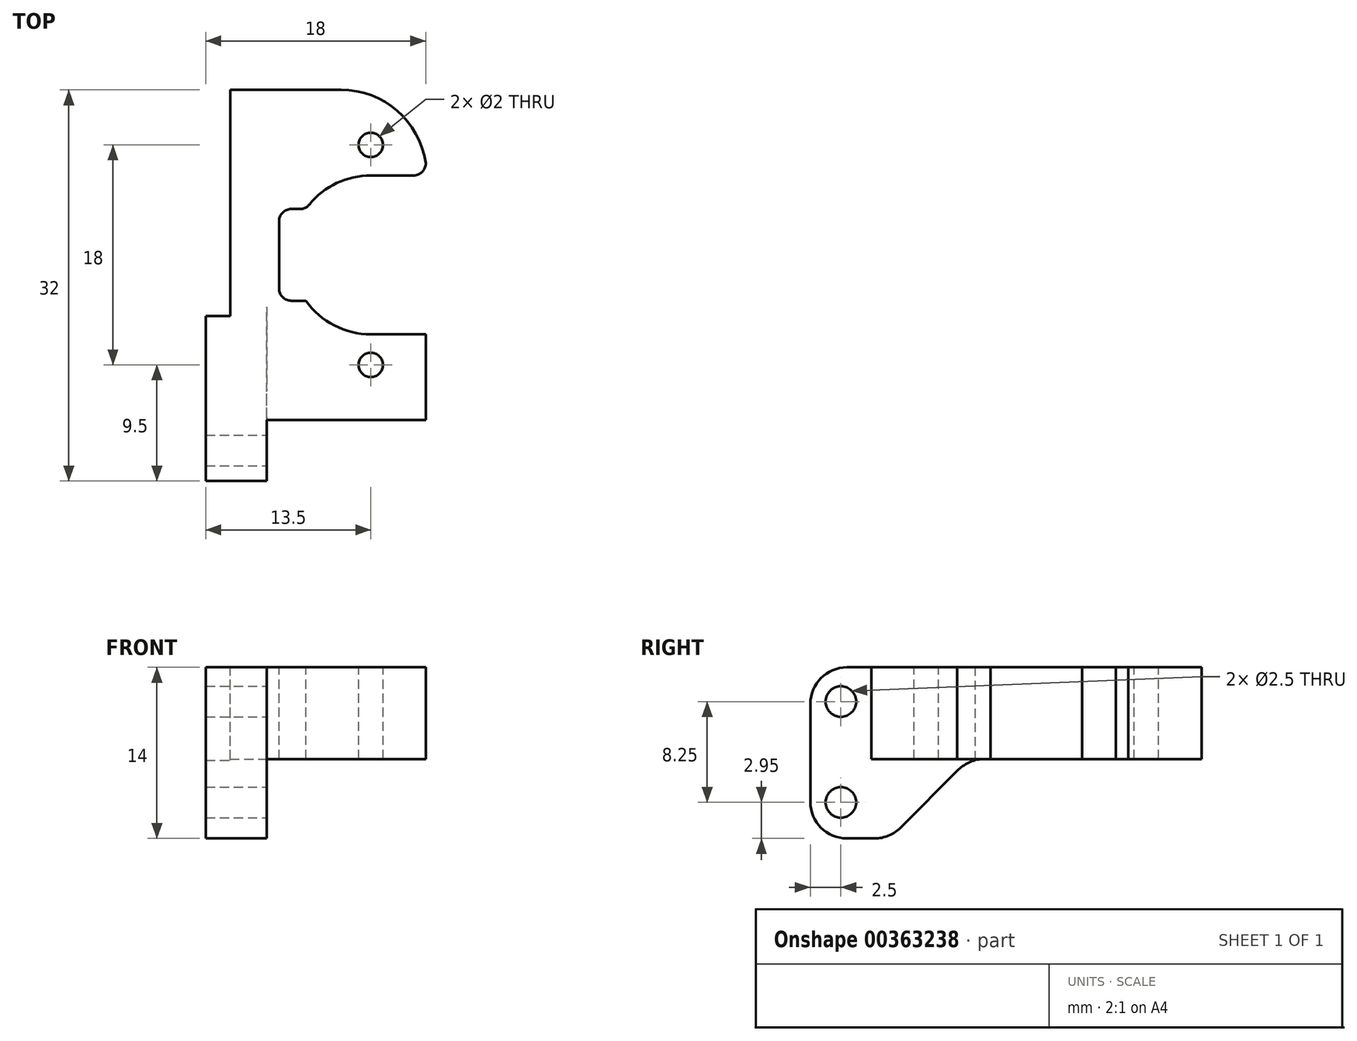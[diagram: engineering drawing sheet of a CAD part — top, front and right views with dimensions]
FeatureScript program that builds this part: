
annotation { "Feature Type Name" : "Feature", "Feature Type Description" : "" }
export const myFeature = defineFeature(function(context is Context, id is Id, definition is map)
    precondition{}
    {
        {
            var Q0;
            Q0=qCreatedBy(makeId("Top.planeOp"),FACE);
            var sketch = newSketch(context, id + "F0", { "sketchPlane" : qUnion([Q0])});
            skLineSegment(sketch, "E0.bottom", {"start": v(0, 0) * mm, "end": v(18, 0) * mm});
            skLineSegment(sketch, "E0.top", {"start": v(0, 32) * mm, "end": v(18, 32) * mm});
            skLineSegment(sketch, "E0.left", {"start": v(0, 0) * mm, "end": v(0, 32) * mm});
            skLineSegment(sketch, "E0.right", {"start": v(18, 0) * mm, "end": v(18, 32) * mm});
            skSolve(sketch);
        }
        {
            var Q0;
            Q0=qSketchRegion(id+"F0",true);
            extrude(context, id + "F1", {"entities" : qUnion([Q0]), "depth" : 14 * mm});
        }
        {
            var Q0;
            Q0=makeQuery(id+"F1.opExtrude","CAP_FACE",FACE,{"disambiguationData":[OSD([sQuery(id+"F0.wireOp",EDGE,"E0.bottom"),sQuery(id+"F0.wireOp",EDGE,"E0.top"),sQuery(id+"F0.wireOp",EDGE,"E0.left"),sQuery(id+"F0.wireOp",EDGE,"E0.right")])],"isStart":false});
            var sketch = newSketch(context, id + "F2", { "sketchPlane" : qUnion([Q0])});
            skLineSegment(sketch, "E1.bottom", {"start": v(5, 0) * mm, "end": v(18, 0) * mm});
            skLineSegment(sketch, "E1.top", {"start": v(5, 5) * mm, "end": v(18, 5) * mm});
            skLineSegment(sketch, "E1.left", {"start": v(5, 0) * mm, "end": v(5, 5) * mm});
            skLineSegment(sketch, "E1.right", {"start": v(18, 0) * mm, "end": v(18, 5) * mm});
            skLineSegment(sketch, "E2.bottom", {"start": v(0, 32) * mm, "end": v(2, 32) * mm});
            skLineSegment(sketch, "E2.top", {"start": v(0, 13.5) * mm, "end": v(2, 13.5) * mm});
            skLineSegment(sketch, "E2.left", {"start": v(0, 32) * mm, "end": v(0, 13.5) * mm});
            skLineSegment(sketch, "E2.right", {"start": v(2, 32) * mm, "end": v(2, 13.5) * mm});
            skSolve(sketch);
        }
        {
            var Q0;
            Q0=qSketchRegion(id+"F2",true);
            extrude(context, id + "F3", {"entities" : qUnion([Q0]), "operationType" : NewBodyOperationType.REMOVE, "endBound" : BoundingType.UP_TO_NEXT, "oppositeDirection" : true, "depth" : 25 * mm});
        }
        {
            var Q0;
            Q0=makeQuery(id+"F1.opExtrude","SWEPT_FACE",FACE,{"disambiguationData":[OSD([sQuery(id+"F0.wireOp",EDGE,"E0.right")])]});
            var sketch = newSketch(context, id + "F4", { "sketchPlane" : qUnion([Q0])});
            skLineSegment(sketch, "E3.bottom", {"start": v(5, 0) * mm, "end": v(32, 0) * mm});
            skLineSegment(sketch, "E3.top", {"start": v(5, 6.5) * mm, "end": v(32, 6.5) * mm});
            skLineSegment(sketch, "E3.left", {"start": v(5, 0) * mm, "end": v(5, 6.5) * mm});
            skLineSegment(sketch, "E3.right", {"start": v(32, 0) * mm, "end": v(32, 6.5) * mm});
            skSolve(sketch);
        }
        {
            var Q0;
            Q0=qSketchRegion(id+"F4",true);
            extrude(context, id + "F5", {"entities" : qUnion([Q0]), "operationType" : NewBodyOperationType.REMOVE, "endBound" : BoundingType.UP_TO_NEXT, "oppositeDirection" : true, "depth" : 25 * mm});
        }
        {
            var Q0;
            Q0=makeQuery(id+"F1.opExtrude","CAP_FACE",FACE,{"disambiguationData":[OSD([sQuery(id+"F0.wireOp",EDGE,"E0.bottom"),sQuery(id+"F0.wireOp",EDGE,"E0.top"),sQuery(id+"F0.wireOp",EDGE,"E0.left"),sQuery(id+"F0.wireOp",EDGE,"E0.right")])],"isStart":false});
            var sketch = newSketch(context, id + "F6", { "sketchPlane" : qUnion([Q0])});
            skLineSegment(sketch, "E4", {"start": v(13.5, 32) * mm, "end": v(13.5, 5) * mm, "construction": true});
            skCircle(sketch, "E5", {"center": v(13.5, 27.5) * mm, "radius": 1 * mm});
            skCircle(sketch, "E6", {"center": v(13.5, 9.5) * mm, "radius": 1 * mm});
            skCircle(sketch, "E7", {"center": v(13.5, 18.5) * mm, "radius": 6.5 * mm});
            skPoint(sketch, "E8", {"position": v(13.5, 25) * mm});
            skPoint(sketch, "E9", {"position": v(13.5, 12) * mm});
            skLineSegment(sketch, "E10", {"start": v(13.5, 25) * mm, "end": v(18, 25) * mm});
            skLineSegment(sketch, "E11", {"start": v(18, 25) * mm, "end": v(18, 12) * mm});
            skLineSegment(sketch, "E12", {"start": v(18, 12) * mm, "end": v(13.5, 12) * mm});
            skSolve(sketch);
        }
        {
            var Q0;
            Q0=makeQuery(id+"F6.imprint","IMPRINT",FACE,{"disambiguationData":[TD([[makeQuery(id+"F6.imprint","IMPRINT",EDGE,{"derivedFrom":sQuery(id+"F6.wireOp",EDGE,"E6")}),1.0]])]});
            var Q1;
            Q1=makeQuery(id+"F6.imprint","IMPRINT",FACE,{"disambiguationData":[TD([[makeQuery(id+"F6.imprint","IMPRINT",EDGE,{"derivedFrom":sQuery(id+"F6.wireOp",EDGE,"E7")}),1.0]])]});
            var Q2;
            Q2=makeQuery(id+"F6.imprint","IMPRINT",FACE,{"disambiguationData":[TD([[makeQuery(id+"F6.imprint","IMPRINT",EDGE,{"derivedFrom":sQuery(id+"F6.wireOp",EDGE,"E5")}),1.0]])]});
            var Q3;
            {var subQ0=sQuery(id+"F6.wireOp",EDGE,"E10");Q3=makeQuery(id+"F6.imprint","IMPRINT",FACE,{"disambiguationData":[TD([[makeQuery(id+"F6.imprint","IMPRINT",EDGE,{"derivedFrom":subQ0}),-1.0]])]});}
            var Q4;
            {var subQ0=sQuery(id+"F6.wireOp",EDGE,"E12");Q4=makeQuery(id+"F6.imprint","IMPRINT",FACE,{"disambiguationData":[TD([[makeQuery(id+"F6.imprint","IMPRINT",EDGE,{"derivedFrom":subQ0}),-1.0]])]});}
            extrude(context, id + "F7", {"entities" : qUnion([Q0, Q1, Q2, Q3, Q4]), "operationType" : NewBodyOperationType.REMOVE, "endBound" : BoundingType.UP_TO_NEXT, "oppositeDirection" : true, "depth" : 25 * mm});
        }
        {
            var Q0;
            Q0=makeQuery(id+"F3.boolean.opBoolean","COPY",FACE,{"derivedFrom":makeQuery(id+"F3.opExtrude","SWEPT_FACE",FACE,{"disambiguationData":[OSD([sQuery(id+"F2.wireOp",EDGE,"E1.left")])]})});
            var sketch = newSketch(context, id + "F8", { "sketchPlane" : qUnion([Q0])});
            skCircle(sketch, "E13", {"center": v(2.5, 11.2) * mm, "radius": 1.25 * mm});
            skPoint(sketch, "E13.centerSnap0", {"position": v(2.5, 14) * mm});
            skCircle(sketch, "E14", {"center": v(2.5, 2.95) * mm, "radius": 1.25 * mm});
            skPoint(sketch, "E14.centerSnap0", {"position": v(2.5, 0) * mm});
            skSolve(sketch);
        }
        {
            var Q0;
            Q0=qSketchRegion(id+"F8",true);
            extrude(context, id + "F9", {"entities" : qUnion([Q0]), "operationType" : NewBodyOperationType.REMOVE, "endBound" : BoundingType.UP_TO_NEXT, "oppositeDirection" : true, "depth" : 25 * mm});
        }
        {
            var Q0;
            {var subQ0=sQuery(id+"F4.wireOp",EDGE,"E3.top");var subQ1=sQuery(id+"F2.wireOp",EDGE,"E1.top");var subQ2=sQuery(id+"F4.wireOp",EDGE,"E3.left");Q0=makeQuery(id+"F5.boolean.opBoolean","COPY",EDGE,{"disambiguationData":[TD([makeQuery(id+"F1.opExtrude","SWEPT_FACE",FACE,{"disambiguationData":[OSD([sQuery(id+"F0.wireOp",EDGE,"E0.left")])]})])],"derivedFrom":makeQuery(id+"F5.opExtrude","SWEPT_EDGE",EDGE,{"disambiguationData":[OSD([sQuery(id+"F0.wireOp",EDGE,"E0.right"),subQ1,sQuery(id+"F2.wireOp",EDGE,"E1.right"),subQ0,subQ2])]})});}
            chamfer(context, id + "F10", {"entities" : qUnion([Q0]), "width" : 8 * mm, "tangentPropagation" : true});
        }
        {
            var Q0;
            Q0=makeQuery(id+"F1.opExtrude","CAP_EDGE",EDGE,{"disambiguationData":[OSD([sQuery(id+"F0.wireOp",EDGE,"E0.bottom")])],"isStart":false});
            var Q1;
            Q1=makeQuery(id+"F1.opExtrude","CAP_EDGE",EDGE,{"disambiguationData":[OSD([sQuery(id+"F0.wireOp",EDGE,"E0.bottom")])],"isStart":true});
            var Q2;
            {var subQ0=sQuery(id+"F0.wireOp",EDGE,"E0.right");var subQ1=sQuery(id+"F0.wireOp",EDGE,"E0.left");var subQ2=sQuery(id+"F4.wireOp",EDGE,"E3.top");var subQ3=sQuery(id+"F2.wireOp",EDGE,"E1.top");var subQ4=sQuery(id+"F4.wireOp",EDGE,"E3.left");Q2=makeQuery(id+"F10.opChamfer","BLEND_EDGE",EDGE,{"blendedFrom":[makeQuery(id+"F5.boolean.opBoolean","COPY",EDGE,{"disambiguationData":[TD([makeQuery(id+"F1.opExtrude","SWEPT_FACE",FACE,{"disambiguationData":[OSD([subQ1])]})])],"derivedFrom":makeQuery(id+"F5.opExtrude","SWEPT_EDGE",EDGE,{"disambiguationData":[OSD([subQ0,subQ3,sQuery(id+"F2.wireOp",EDGE,"E1.right"),subQ2,subQ4])]})}),makeQuery(id+"F1.opExtrude","CAP_FACE",FACE,{"disambiguationData":[OSD([sQuery(id+"F0.wireOp",EDGE,"E0.bottom"),sQuery(id+"F0.wireOp",EDGE,"E0.top"),subQ1,subQ0])],"isStart":true})],"blendedInto":[makeQuery(id+"F1.opExtrude","CAP_FACE",FACE,{"disambiguationData":[OSD([sQuery(id+"F0.wireOp",EDGE,"E0.bottom"),sQuery(id+"F0.wireOp",EDGE,"E0.top"),subQ1,subQ0])],"isStart":true})]});}
            var Q3;
            {var subQ0=sQuery(id+"F4.wireOp",EDGE,"E3.top");var subQ1=makeQuery(id+"F5.opExtrude","SWEPT_FACE",FACE,{"disambiguationData":[OSD([subQ0])]});var subQ2=sQuery(id+"F2.wireOp",EDGE,"E1.top");var subQ3=sQuery(id+"F4.wireOp",EDGE,"E3.left");Q3=makeQuery(id+"F10.opChamfer","BLEND_EDGE",EDGE,{"blendedFrom":[makeQuery(id+"F5.boolean.opBoolean","COPY",EDGE,{"disambiguationData":[TD([makeQuery(id+"F1.opExtrude","SWEPT_FACE",FACE,{"disambiguationData":[OSD([sQuery(id+"F0.wireOp",EDGE,"E0.left")])]})])],"derivedFrom":makeQuery(id+"F5.opExtrude","SWEPT_EDGE",EDGE,{"disambiguationData":[OSD([sQuery(id+"F0.wireOp",EDGE,"E0.right"),subQ2,sQuery(id+"F2.wireOp",EDGE,"E1.right"),subQ0,subQ3])]})}),makeQuery(id+"F5.boolean.opBoolean","COPY",FACE,{"derivedFrom":subQ1})],"blendedInto":[makeQuery(id+"F5.boolean.opBoolean","COPY",FACE,{"derivedFrom":subQ1})]});}
            fillet(context, id + "F11", {"entities" : qUnion([Q0, Q1, Q2, Q3]), "radius" : 3 * mm, "tangentPropagation" : true, "allowEdgeOverflow" : false});
        }
        {
            var Q0;
            Q0=makeQuery(id+"F7.boolean.opBoolean","COPY",EDGE,{"derivedFrom":makeQuery(id+"F7.opExtrude","SWEPT_EDGE",EDGE,{"disambiguationData":[OSD([sQuery(id+"F0.wireOp",EDGE,"E0.right"),sQuery(id+"F6.wireOp",EDGE,"E11"),sQuery(id+"F6.wireOp",EDGE,"E12")])]})});
            var Q1;
            Q1=makeQuery(id+"F7.boolean.opBoolean","COPY",EDGE,{"derivedFrom":makeQuery(id+"F7.opExtrude","SWEPT_EDGE",EDGE,{"disambiguationData":[OSD([sQuery(id+"F0.wireOp",EDGE,"E0.right"),sQuery(id+"F6.wireOp",EDGE,"E10"),sQuery(id+"F6.wireOp",EDGE,"E11")])]})});
            fillet(context, id + "F12", {"entities" : qUnion([Q0, Q1]), "radius" : 1 * mm, "tangentPropagation" : true, "allowEdgeOverflow" : false});
        }
        {
            var Q0;
            Q0=makeQuery(id+"F3.boolean.opBoolean","COPY",EDGE,{"derivedFrom":makeQuery(id+"F3.opExtrude","SWEPT_EDGE",EDGE,{"disambiguationData":[OSD([sQuery(id+"F0.wireOp",EDGE,"E0.right"),sQuery(id+"F2.wireOp",EDGE,"E1.top"),sQuery(id+"F2.wireOp",EDGE,"E1.right")])]})});
            var Q1;
            Q1=makeQuery(id+"F1.opExtrude","SWEPT_EDGE",EDGE,{"disambiguationData":[OSD([sQuery(id+"F0.wireOp",EDGE,"E0.top"),sQuery(id+"F0.wireOp",EDGE,"E0.right")])]});
            var Q2;
            Q2=makeQuery(id+"F1.opExtrude","SWEPT_EDGE",EDGE,{"disambiguationData":[OSD([sQuery(id+"F0.wireOp",EDGE,"E0.top"),sQuery(id+"F0.wireOp",EDGE,"E0.left")])]});
            var Q3;
            Q3=makeQuery(id+"F3.boolean.opBoolean","COPY",EDGE,{"derivedFrom":makeQuery(id+"F3.opExtrude","SWEPT_EDGE",EDGE,{"disambiguationData":[OSD([sQuery(id+"F0.wireOp",EDGE,"E0.top"),sQuery(id+"F2.wireOp",EDGE,"E2.bottom"),sQuery(id+"F2.wireOp",EDGE,"E2.right")])]})});
            fillet(context, id + "F13", {"entities" : qUnion([Q0, Q1, Q2, Q3]), "radius" : 7 * mm, "tangentPropagation" : true, "allowEdgeOverflow" : false});
        }
        {
            var Q0;
            Q0=makeQuery(id+"F1.opExtrude","CAP_FACE",FACE,{"disambiguationData":[OSD([sQuery(id+"F0.wireOp",EDGE,"E0.bottom"),sQuery(id+"F0.wireOp",EDGE,"E0.top"),sQuery(id+"F0.wireOp",EDGE,"E0.left"),sQuery(id+"F0.wireOp",EDGE,"E0.right")])],"isStart":false});
            var sketch = newSketch(context, id + "F14", { "sketchPlane" : qUnion([Q0])});
            skLineSegment(sketch, "E15", {"start": v(7, 18.5) * mm, "end": v(3.7, 18.5) * mm, "construction": true});
            skLineSegment(sketch, "E16.bottom", {"start": v(8.2, 22.25) * mm, "end": v(6, 22.25) * mm});
            skLineSegment(sketch, "E16.top", {"start": v(8.2, 14.75) * mm, "end": v(6, 14.75) * mm});
            skLineSegment(sketch, "E16.left", {"start": v(8.2, 22.25) * mm, "end": v(8.2, 14.75) * mm});
            skLineSegment(sketch, "E16.right", {"start": v(6, 22.25) * mm, "end": v(6, 14.75) * mm});
            skPoint(sketch, "E16.middle", {"position": v(7.1, 18.5) * mm});
            skSolve(sketch);
        }
        {
            var Q0;
            {var subQ0=sQuery(id+"F14.wireOp",EDGE,"E16.bottom");Q0=makeQuery(id+"F14.imprint","IMPRINT",FACE,{"disambiguationData":[TD([[makeQuery(id+"F14.imprint","IMPRINT",EDGE,{"derivedFrom":subQ0}),1.0]])]});}
            extrude(context, id + "F15", {"entities" : qUnion([Q0]), "operationType" : NewBodyOperationType.REMOVE, "endBound" : BoundingType.THROUGH_ALL, "oppositeDirection" : true, "depth" : 25 * mm});
        }
        {
            var Q0;
            Q0=makeQuery(id+"F15.boolean.opBoolean","COPY",EDGE,{"derivedFrom":makeQuery(id+"F15.opExtrude","SWEPT_EDGE",EDGE,{"disambiguationData":[OSD([sQuery(id+"F14.wireOp",EDGE,"E16.top"),sQuery(id+"F14.wireOp",EDGE,"E16.right")])]})});
            var Q1;
            Q1=makeQuery(id+"F15.boolean.opBoolean","COPY",EDGE,{"derivedFrom":makeQuery(id+"F15.opExtrude","SWEPT_EDGE",EDGE,{"disambiguationData":[OSD([sQuery(id+"F14.wireOp",EDGE,"E16.bottom"),sQuery(id+"F14.wireOp",EDGE,"E16.right")])]})});
            var Q2;
            Q2=makeQuery(id+"F15.boolean.opBoolean","COPY",EDGE,{"derivedFrom":makeQuery(id+"F15.opExtrude","SWEPT_EDGE",EDGE,{"disambiguationData":[OSD([sQuery(id+"F6.wireOp",EDGE,"E7"),sQuery(id+"F14.wireOp",EDGE,"E16.bottom"),sQuery(id+"F14.wireOp",EDGE,"E16.left")])]})});
            var Q3;
            Q3=makeQuery(id+"F15.boolean.opBoolean","COPY",EDGE,{"derivedFrom":makeQuery(id+"F15.opExtrude","SWEPT_EDGE",EDGE,{"disambiguationData":[OSD([sQuery(id+"F6.wireOp",EDGE,"E7"),sQuery(id+"F14.wireOp",EDGE,"E16.top"),sQuery(id+"F14.wireOp",EDGE,"E16.left")])]})});
            var Q4;
            Q4=makeQuery(id+"F3.boolean.opBoolean","COPY",EDGE,{"derivedFrom":makeQuery(id+"F3.opExtrude","SWEPT_EDGE",EDGE,{"disambiguationData":[OSD([sQuery(id+"F0.wireOp",EDGE,"E0.left"),sQuery(id+"F2.wireOp",EDGE,"E2.top"),sQuery(id+"F2.wireOp",EDGE,"E2.left")])]})});
            fillet(context, id + "F16", {"entities" : qUnion([Q0, Q1, Q2, Q3, Q4]), "radius" : 1 * mm, "tangentPropagation" : true, "allowEdgeOverflow" : false});
        }
    });
